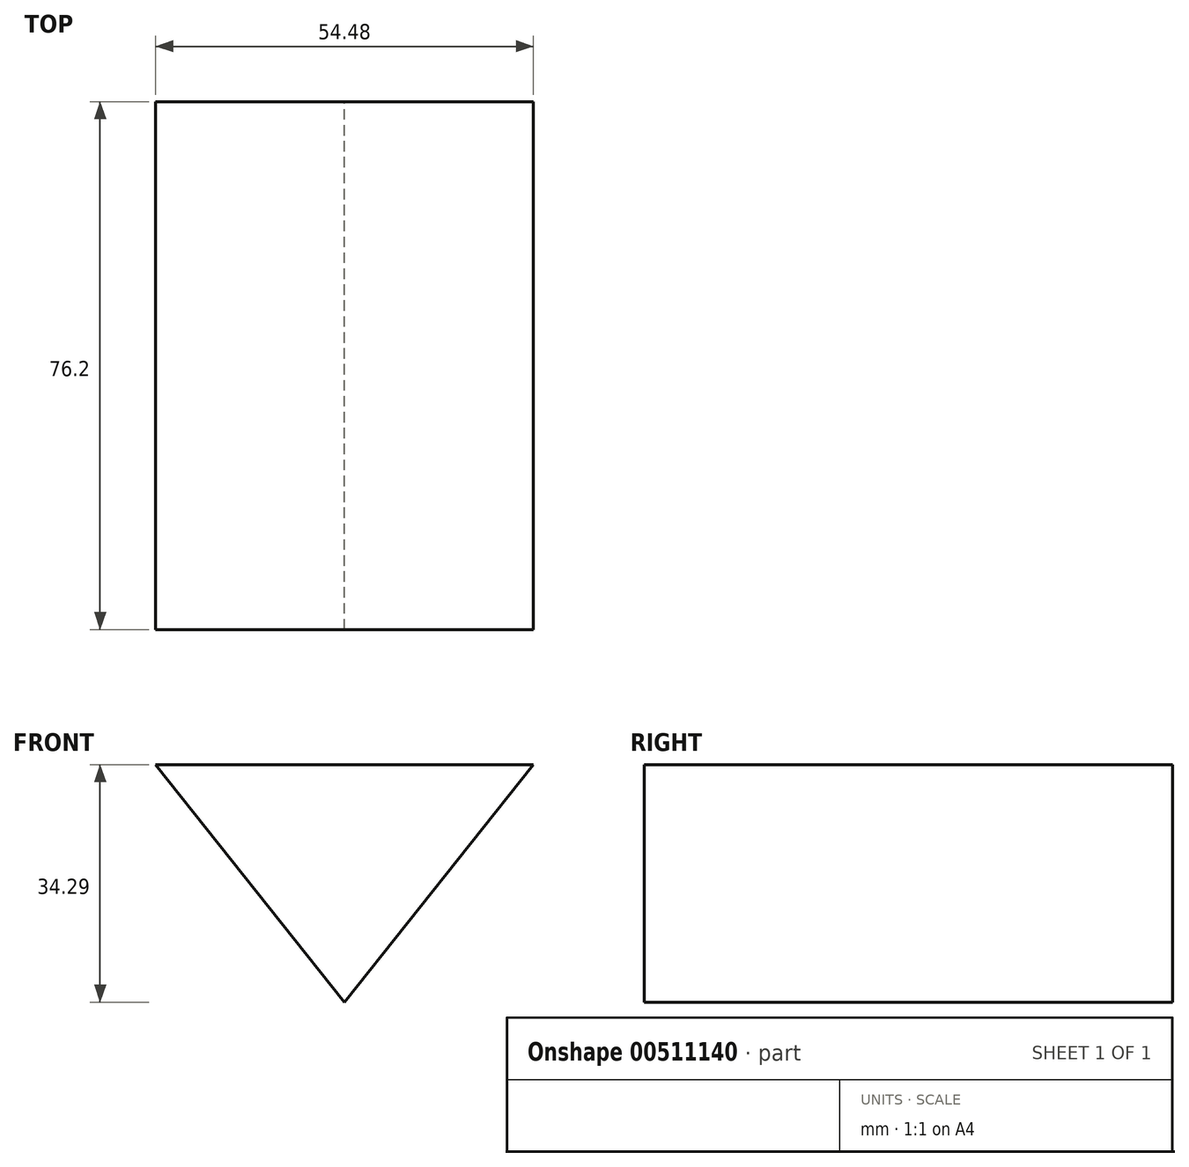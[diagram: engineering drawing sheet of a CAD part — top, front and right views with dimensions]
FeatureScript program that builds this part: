
annotation { "Feature Type Name" : "Feature", "Feature Type Description" : "" }
export const myFeature = defineFeature(function(context is Context, id is Id, definition is map)
    precondition{}
    {
        {
            var Q0;
            Q0=qCreatedBy(makeId("Front.planeOp"),FACE);
            var sketch = newSketch(context, id + "F0", { "sketchPlane" : qUnion([Q0])});
            skLineSegment(sketch, "E0", {"start": v(-62.35, 45.08) * mm, "end": v(-7.87, 45.08) * mm});
            skLineSegment(sketch, "E1", {"start": v(-35.11, 45.08) * mm, "end": v(-35.11, 10.8) * mm, "construction": true});
            skLineSegment(sketch, "E2", {"start": v(-35.11, 10.8) * mm, "end": v(-62.35, 45.08) * mm});
            skLineSegment(sketch, "E3", {"start": v(-35.11, 10.8) * mm, "end": v(-7.87, 45.08) * mm});
            skSolve(sketch);
        }
        {
            var Q0;
            Q0=makeQuery(id+"F0.imprint","IMPRINT",FACE,{"disambiguationData":[TD([[makeQuery(id+"F0.imprint","IMPRINT",EDGE,{"derivedFrom":sQuery(id+"F0.wireOp",EDGE,"E0")}),-1.0]])]});
            extrude(context, id + "F1", {"entities" : qUnion([Q0]), "depth" : 76.2 * mm});
        }
    });
